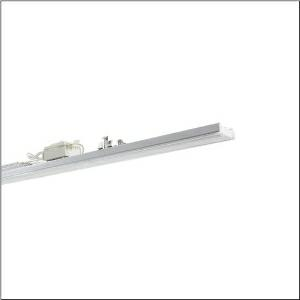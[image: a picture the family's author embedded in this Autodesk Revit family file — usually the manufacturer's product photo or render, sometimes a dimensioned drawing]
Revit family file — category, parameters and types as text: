
# Revit family: licross_r__21_recessed_mo_52tl12de45xg_f928
name_source: partatom
category: Lighting Fixtures
units: mm (PartAtom-declared; Revit-internal decimal feet)

## family parameters
Cut with Voids When Loaded = No
Host = Face
Light Source = No
Part Type = Normal
Room Calculation Point = No
Round Connector Dimension = Use Diameter
Shared = No

## types (1)
- --- (1 x LED, 5140 lm, 29.9 W, 4000K)
    Apparent Load = 30 VA
    CIE Flux Codes = 72 92 99 100 100
    Color Rendering = 80
    Color Temperature = 4000K
    Default Elevation = 1800 mm
    Description = Licross® 21 Recessed MO, luminaire insert, of sheet steel, galvanised, coil coated, white, length: 750mm, width: 66mm, height: 67mm, LED rated luminous flux: 5.140lm, light colour: 840, control gear: DALI 2, with plug, 5-pole, with phase selection, mains connection: 220..240V, AC, 50/60Hz, rated input power: 30W, halogen-free wiring, primary light control with lens, of plastic, primary optical cover: cover, of PMMA, light emission: direct distribution, primary light characteristic: symmetric, protection rating (complete): IP40, insulation class (complete): insulation class I (protective earthing), certification: CE, ENEC, VDE, UKCA, protection symbol: D if used in an environment without relevant dust loads with corresponding accessories, impact resistance: IK06, permissible ambient temperature for indoor applications: -25..+35°C, corresponds to IFS (International Featured Standards) requirements for safety and quality in the food industry, reducing of maximum allowable ambient temperature of 5°C with ceiling mounting, LABS conformity tested according to VDMA 24364:2018-05, packaging unit: 1 piece
    Height = 58 mm
    Lamp = 1 x LED
    Lamp Light Flux = 5140 lm
    Lamp Power = 29.9 W
    Lamp count = 1
    Length = 750 mm
    Luminous efficacy = 172 lm/W
    Manufacturer = Siteco
    ModVariant = No
    Model = 52TL12DE45XG
    Mounting Place = Ceiling
    Mounting Type = Pendant
    Number of Poles = 1
    OnlyDefault = Yes
    Power Factor = 1
    Product Name = Licross® 21 Recessed MO
    Product group = luminaire insert
    ProductGroupID = 902
    Protection Class = Protection class I
    Protection Degree = IP 40
    RLX_Detail_Level = 1
    RLX_Emergency_Light_Flux = 0 lm
    RLX_Emergency_Type = 0
    RLX_Emergency_Type_DB = No
    RlxData = <blob elided: 28957 chars, md5=e5d043e0>
    Socket = socket
    Standby Power = 0 W
    System Light Flux = 5140 lm
    System Power = 30 W
    Type Comments = factory setting: luminous flux: 100 % | dim-lin: 254 | 390 mA
    Type Image = l_1296930.jpg
    URL = http://relux.com
    VarID = @adj_126538
    Voltage = 0 V
    Weight = 0.00 kg
    Width = 66 mm

## geometry (parser evidence)
native form markers: Blend x4, Sweep x11
no freeform markers — native parametric forms only
